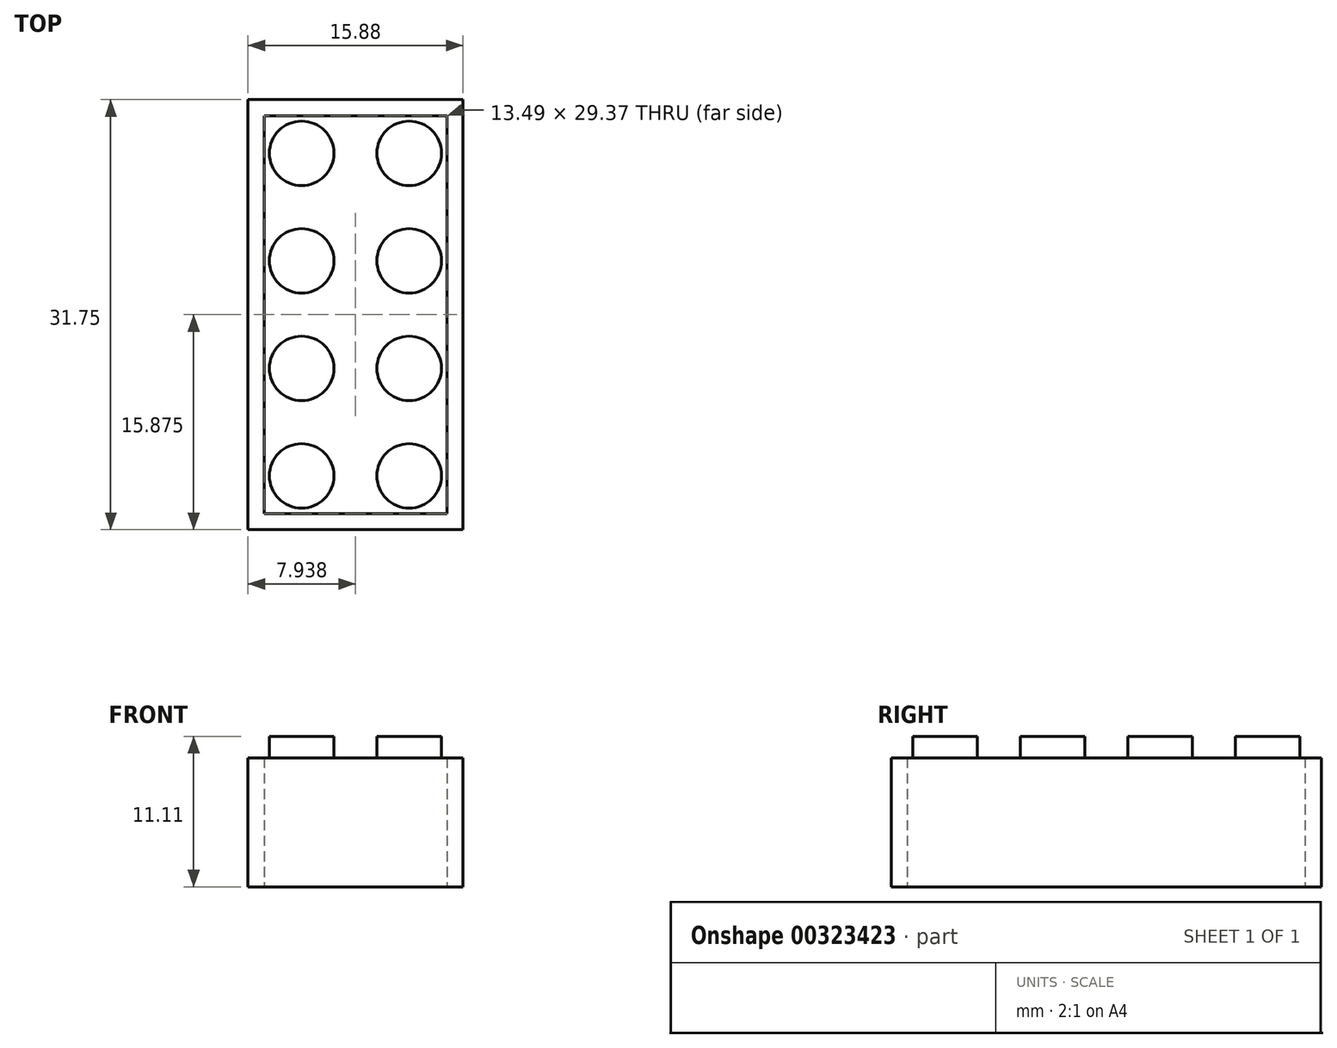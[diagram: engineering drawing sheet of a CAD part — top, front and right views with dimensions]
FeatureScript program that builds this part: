
annotation { "Feature Type Name" : "Feature", "Feature Type Description" : "" }
export const myFeature = defineFeature(function(context is Context, id is Id, definition is map)
    precondition{}
    {
        {
            var Q0;
            Q0=qCreatedBy(makeId("Top.planeOp"),FACE);
            var sketch = newSketch(context, id + "F0", { "sketchPlane" : qUnion([Q0])});
            skLineSegment(sketch, "E0", {"start": v(0, 0) * mm, "end": v(0, 31.75) * mm});
            skLineSegment(sketch, "E1", {"start": v(0, 31.75) * mm, "end": v(15.87, 31.75) * mm});
            skLineSegment(sketch, "E2", {"start": v(15.87, 31.75) * mm, "end": v(15.88, 0) * mm});
            skLineSegment(sketch, "E3", {"start": v(15.88, 0) * mm, "end": v(0, 0) * mm});
            skLineSegment(sketch, "E4.0", {"start": v(14.68, 30.56) * mm, "end": v(14.68, 1.2) * mm});
            skLineSegment(sketch, "E4.1", {"start": v(1.2, 30.56) * mm, "end": v(14.68, 30.56) * mm});
            skLineSegment(sketch, "E4.2", {"start": v(1.2, 1.2) * mm, "end": v(1.2, 30.56) * mm});
            skLineSegment(sketch, "E4.3", {"start": v(14.68, 1.2) * mm, "end": v(1.2, 1.2) * mm});
            skSolve(sketch);
        }
        {
            var Q0;
            Q0=makeQuery(id+"F0.imprint","IMPRINT",FACE,{"disambiguationData":[TD([[makeQuery(id+"F0.imprint","IMPRINT",EDGE,{"derivedFrom":sQuery(id+"F0.wireOp",EDGE,"E0")}),-1.0]])]});
            extrude(context, id + "F1", {"entities" : qUnion([Q0]), "depth" : 9.52 * mm});
        }
        {
            var Q0;
            Q0=makeQuery(id+"F1.opExtrude","CAP_FACE",FACE,{"disambiguationData":[OSD([sQuery(id+"F0.wireOp",EDGE,"E0"),sQuery(id+"F0.wireOp",EDGE,"E1"),sQuery(id+"F0.wireOp",EDGE,"E2"),sQuery(id+"F0.wireOp",EDGE,"E3")])],"isStart":false});
            var sketch = newSketch(context, id + "F2", { "sketchPlane" : qUnion([Q0])});
            skPoint(sketch, "E5", {"position": v(3.97, 27.79) * mm});
            skPoint(sketch, "E6", {"position": v(11.9, 27.79) * mm});
            skPoint(sketch, "E7", {"position": v(11.9, 19.85) * mm});
            skPoint(sketch, "E8", {"position": v(3.97, 19.85) * mm});
            skPoint(sketch, "E9", {"position": v(11.9, 11.91) * mm});
            skPoint(sketch, "E10", {"position": v(11.9, 3.98) * mm});
            skPoint(sketch, "E11", {"position": v(3.97, 3.98) * mm});
            skPoint(sketch, "E12", {"position": v(3.97, 11.91) * mm});
            skCircle(sketch, "E13", {"center": v(3.97, 27.79) * mm, "radius": 2.38 * mm});
            skCircle(sketch, "E14", {"center": v(11.9, 27.79) * mm, "radius": 2.38 * mm});
            skCircle(sketch, "E15", {"center": v(3.97, 19.85) * mm, "radius": 2.38 * mm});
            skCircle(sketch, "E16", {"center": v(11.9, 19.85) * mm, "radius": 2.38 * mm});
            skCircle(sketch, "E17", {"center": v(3.97, 11.91) * mm, "radius": 2.38 * mm});
            skCircle(sketch, "E18", {"center": v(11.9, 11.91) * mm, "radius": 2.38 * mm});
            skCircle(sketch, "E19", {"center": v(3.97, 3.98) * mm, "radius": 2.38 * mm});
            skCircle(sketch, "E20", {"center": v(11.9, 3.98) * mm, "radius": 2.38 * mm});
            skSolve(sketch);
        }
        {
            var Q0;
            Q0 = qSketchRegion(id + "F2", true);
            extrude(context, id + "F3", {"entities" : qUnion([Q0]), "operationType" : NewBodyOperationType.ADD, "depth" : 1.59 * mm});
        }
    });
